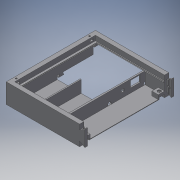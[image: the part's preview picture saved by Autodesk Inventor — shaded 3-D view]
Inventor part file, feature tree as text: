
AUTODESK INVENTOR PART (.ipt)
format: ipt  version: 2016 SP2 (Build 200236200, 236)  size: 1,031,680 bytes
history: native  units: mm
features: sketch x28, extrude x24, reference x10, projected_geometry x6, chamfer x2, thread x2, revolve x2, other x2
ambient origin geometry x8: Origin, YZ Plane, XZ Plane, XY Plane, X Axis, Y Axis, Z Axis, Center Point
bodies: Volumenkörper1 (feature_tree), Volumenkörper4 (feature_tree), Volumenkörper5 (feature_tree)
feature tree (76):
  extrude  "Extrusion1"  Depth=2.0mm TaperAngle=0.0deg
  extrude  "Extrusion2"  Depth=26.0mm TaperAngle=0.0deg
  chamfer  "Fase1"  Distance=3.0mm
  extrude  "Extrusion3"  Depth=78.5mm
  extrude  "Extrusion4"  Depth=2.5mm
  extrude  "Extrusion5"  Depth=43.5mm
  extrude  "Extrusion8"  Depth=0.5mm
  extrude  "Extrusion9"  Depth=23.0mm TaperAngle=0.0deg
  extrude  "Extrusion10"  Depth=12.0mm
  extrude  "Extrusion11"  Depth=12.0mm
  extrude  "Extrusion12"  Depth=10.0mm
  extrude  "Extrusion13"  Depth=10.0mm
  extrude  "Extrusion14"  Depth=10.0mm
  extrude  "Extrusion15"  Depth=3.5mm TaperAngle=0.0deg
  extrude  "Extrusion16"  Depth=3.0mm
  extrude  "Extrusion17"  Depth=5.8mm
  extrude  "Extrusion18"  Depth=2.5mm TaperAngle=0.0deg
  extrude  "Extrusion19"  Depth=30.0mm
  extrude  "Extrusion20"  TaperAngle=60.0deg  [1 undecoded]
  extrude  "Extrusion21"  Depth=5.0mm TaperAngle=0.0deg
  extrude  "Extrusion22"  Depth=5.0mm
  extrude  "Extrusion23"  Depth=10.0mm
  extrude  "Extrusion24"  Depth=25.0mm
  thread  "Gewinde3"  [1 undecoded]
  thread  "Gewinde4"  [1 undecoded]
  revolve  "Umdrehung3"
  other  "Spirale3"
  revolve  "Umdrehung4"
  other  "Spirale4"
  extrude  "Extrusion25"  Depth=3.0mm
  extrude  "Extrusion26"  Depth=3.0mm
  chamfer  "Fase2"  Distance=7.0mm
  sketch  "Skizze1"  dims[d0=9.3mm d1=0.0mm d2=2.0mm d3=0.0mm]
  reference  "Referenz1"
  reference  "Referenz2"
  reference  "Referenz3"
  sketch  "Skizze2"  dims[d4=1.5mm d5=2.0mm d6=45.0deg d7=26.0mm d8=0.0mm d9=3.0mm d10=0.0mm]
  reference  "Referenz4"
  sketch  "Skizze3"  dims[d15=2.0mm d16=78.5mm]
  projected_geometry  "Projizierte Kontur1"
  sketch  "Skizze4"  dims[d17=43.5mm d18=2.5mm]
  sketch  "Skizze6"  dims[d20=90.0deg d21=43.5mm]
  sketch  "Skizze9"  dims[d22=3.0mm d23=0.5mm]
  sketch  "Skizze10"  dims[d24=78.5mm d25=23.0mm d26=0.0mm]
  sketch  "Skizze11"  dims[d41=12.0mm d42=12.0mm]
  sketch  "Skizze12"  dims[d43=12.0mm d44=12.0mm]
  projected_geometry  "Projizierte Kontur2"
  projected_geometry  "Projizierte Kontur3"
  sketch  "Skizze13"  dims[d45=8.0mm d46=0.0mm d47=10.0mm]
  sketch  "Skizze14"  dims[d48=2.0mm d49=0.0mm d50=10.0mm]
  sketch  "Skizze15"  dims[d51=10.0mm d52=10.0mm]
  projected_geometry  "Projizierte Kontur4"
  sketch  "Skizze16"  dims[d53=10.0mm d54=3.5mm d55=0.0mm]
  sketch  "Skizze17"  dims[d56=3.0mm d57=3.0mm]
  sketch  "Skizze18"  dims[d62=9.25mm d63=0.0mm d64=5.8mm]
  reference  "Referenz5"
  reference  "Referenz6"
  sketch  "Skizze19"  dims[d65=5.8mm d66=2.5mm d67=0.0mm]
  sketch  "Skizze20"  dims[d68=10.0mm d69=30.0mm]
  reference  "Referenz7"
  reference  "Referenz8"
  sketch  "Skizze21"  dims[d70=60.0deg d71=60.0deg]
  sketch  "Skizze22"  dims[d72=5.0mm d73=0.0mm d74=5.0mm d75=0.0mm]
  projected_geometry  "Projizierte Kontur5"
  sketch  "Skizze27"  dims[d76=5.0mm d77=5.0mm]
  sketch  "Skizze28"  dims[d80=2.5mm d81=0.0mm d82=10.0mm]
  sketch  "Skizze29"  dims[d83=10.0mm d84=25.0mm d85=10.0mm d86=4.0mm d87=0.0mm]
  sketch  "Skizze30"  dims[d88=9.0mm d89=0.0mm d90=3.0mm]
  sketch  "Skizze31"  dims[d91=5.7mm d92=3.0mm]
  sketch  "Skizze32"  dims[d93=5.7mm]
  sketch  "Skizze33"  dims[d94=1.35mm]
  sketch  "Skizze34"  dims[d95=3.5mm d96=7.0mm d97=0.0mm]
  sketch  "Skizze35"  dims[d98=1.35mm d99=62.25mm d100=0.0mm d101=5.7mm d102=2.8mm d103=4.0mm d104=0.0mm d105=4.0mm d106=0.0mm d118=60.0deg d136=60.0deg d150=43.5mm d151=10.0mm d152=15.0mm d153=100.0mm d154=0.0mm d156=5.0mm d157=12.217305mm d158=12.217305mm d159=10.0mm d162=12.217305mm d163=10.0mm d164=12.217305mm d165=2.5mm d166=5.0mm d167=2.5mm d168=6.0mm d169=0.0mm d170=7.0mm d171=7.0mm d172=7.5mm d173=5.0mm d174=5.0mm d175=2.5mm d176=0.0mm d177=10.0mm d178=0.0mm d179=10.0mm d180=0.0mm d181=60.0deg d182=0.240125mm d183=0.240125mm d186=1.5mm d188=60.0deg d190=0.0mm d191=1.5015mm d192=7.0mm d193=10.0mm d194=0.0mm d195=0.0mm d196=0.0mm d197=0.0mm d198=0.0mm d199=60.0deg d200=0.240125mm d201=0.240125mm d204=1.5mm d206=60.0deg d208=0.0mm d209=1.5015mm d210=7.0mm d211=10.0mm d212=0.0mm d213=0.0mm d214=0.0mm d215=0.0mm d216=0.0mm d217=30.0mm d218=9.0mm d219=12.5mm d220=19.0mm d221=12.0mm d222=2.0mm d223=6.5mm d224=10.0mm d225=0.0mm d226=0.75mm d227=0.0mm d228=0.75mm d229=2.0mm d230=45.0deg d231=15.0mm d232=20.5mm]
  projected_geometry  "Projizierte Kontur6"
  reference  "Referenz9"
  reference  "Referenz10"
note: 3 required parameter values undecoded (feature->parameter linkage not recoverable at this tier; creation-order binding heuristic only, values carry confidence <= 0.55)
